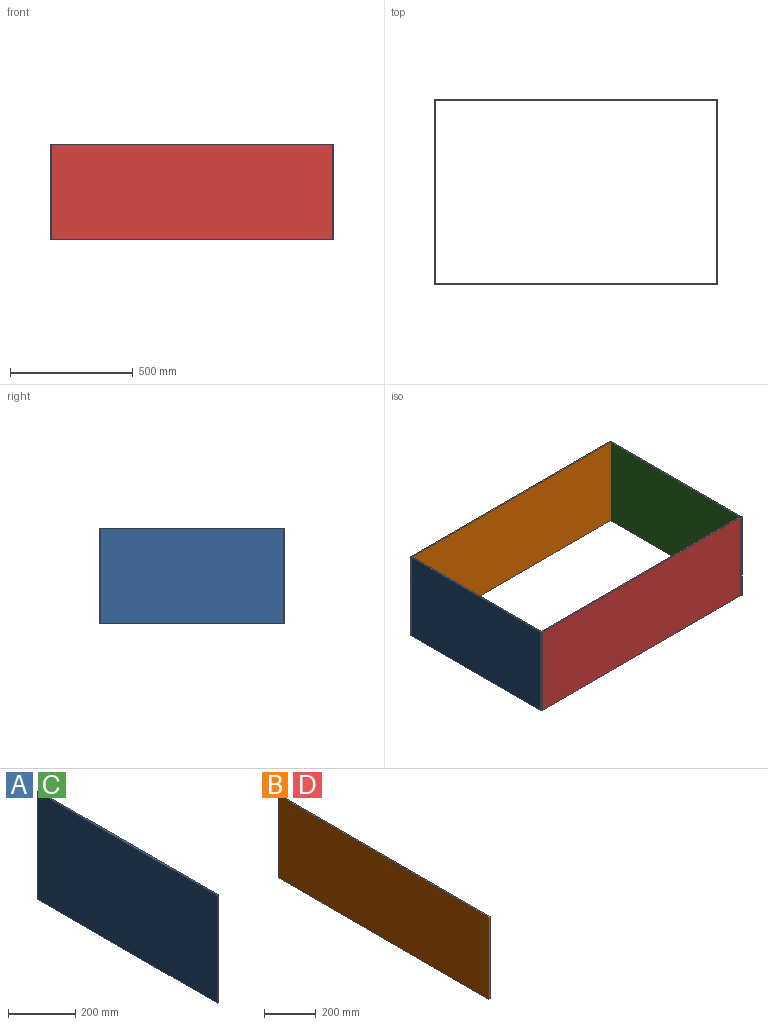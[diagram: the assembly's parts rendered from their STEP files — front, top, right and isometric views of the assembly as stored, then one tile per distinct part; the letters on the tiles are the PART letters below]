
ASSEMBLY  parts=4 mates=1
PART A: 6 faces, bbox 6x755x390 mm
  f0: plane 755x390mm, normal (1,0,0), area 294450mm2, adj f1,f3,f4,f5
  f1: plane 755x6mm, normal (0,0,1), area 4530mm2, adj f0,f2,f4,f5
  f2: plane 755x390mm, normal (-1,0,0), area 294450mm2, adj f1,f3,f4,f5
  f3: plane 755x6mm, normal (0,0,-1), area 4530mm2, adj f0,f2,f4,f5
  f4: plane 390x6mm, normal (0,-1,0), area 2340mm2, adj f0,f1,f2,f3
  f5: plane 390x6mm, normal (0,1,0), area 2340mm2, adj f0,f1,f2,f3
PART B: 6 faces, bbox 6x1155x390 mm
  f0: plane 1155x6mm, normal (0,0,1), area 6930mm2, adj f1,f3,f4,f5
  f1: plane 1155x390mm, normal (-1,0,0), area 450450mm2, adj f0,f2,f4,f5
  f2: plane 1155x6mm, normal (0,0,-1), area 6930mm2, adj f1,f3,f4,f5
  f3: plane 1155x390mm, normal (1,0,0), area 450450mm2, adj f0,f2,f4,f5
  f4: plane 390x6mm, normal (0,-1,0), area 2340mm2, adj f0,f1,f2,f3
  f5: plane 390x6mm, normal (0,1,0), area 2340mm2, adj f0,f1,f2,f3
PART C: same geometry as A
PART D: same geometry as B
PLACE A t=(548.17,247.6,296.75)mm
PLACE B rot(axis=(0,0,1),90deg) t=(245.44,415.15,308.54)mm
PLACE C t=(1697.17,247.6,296.75)mm
PLACE D rot(axis=(0,0,1),90deg) t=(245.44,-333.85,308.54)mm
MATE fastened B.f0 <-> A.f1  axis (0,0,1) through (245.44,247.6,787.16)mm
